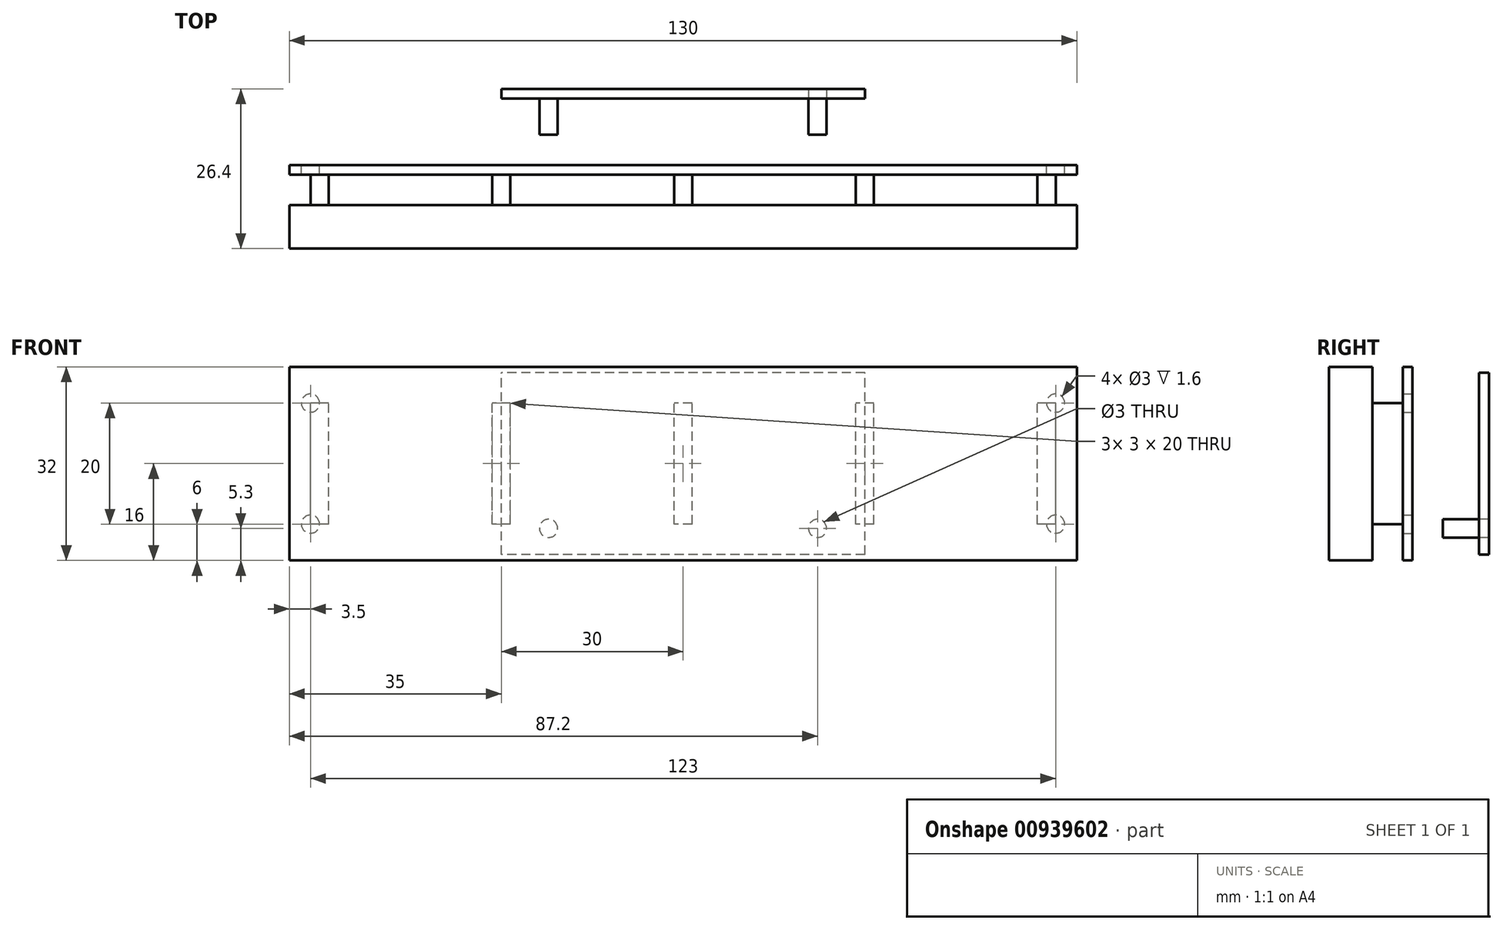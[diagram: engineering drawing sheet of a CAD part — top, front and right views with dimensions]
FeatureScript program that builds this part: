
annotation { "Feature Type Name" : "Feature", "Feature Type Description" : "" }
export const myFeature = defineFeature(function(context is Context, id is Id, definition is map)
    precondition{}
    {
        {
            var Q0;
            Q0=qCreatedBy(makeId("Front.planeOp"),FACE);
            var sketch = newSketch(context, id + "F0", { "sketchPlane" : qUnion([Q0])});
            skLineSegment(sketch, "E0.bottom", {"start": v(65, 16) * mm, "end": v(-65, 16) * mm});
            skLineSegment(sketch, "E0.top", {"start": v(65, -16) * mm, "end": v(-65, -16) * mm});
            skLineSegment(sketch, "E0.left", {"start": v(65, 16) * mm, "end": v(65, -16) * mm});
            skLineSegment(sketch, "E0.right", {"start": v(-65, 16) * mm, "end": v(-65, -16) * mm});
            skPoint(sketch, "E0.middle", {"position": v(0, 0) * mm});
            skSolve(sketch);
        }
        {
            var Q0;
            Q0=makeQuery(id+"F0.imprint","IMPRINT",FACE,{"disambiguationData":[TD([[makeQuery(id+"F0.imprint","IMPRINT",EDGE,{"derivedFrom":sQuery(id+"F0.wireOp",EDGE,"E0.bottom")}),1.0]])]});
            extrude(context, id + "F1", {"entities" : qUnion([Q0]), "depth" : 1.6 * mm, "offsetDistance" : 25 * mm});
        }
        {
            var Q0;
            Q0=makeQuery(id+"F1.opExtrude","CAP_FACE",FACE,{"disambiguationData":[OSD([sQuery(id+"F0.wireOp",EDGE,"E0.bottom"),sQuery(id+"F0.wireOp",EDGE,"E0.top"),sQuery(id+"F0.wireOp",EDGE,"E0.left"),sQuery(id+"F0.wireOp",EDGE,"E0.right")])],"isStart":false});
            var sketch = newSketch(context, id + "F2", { "sketchPlane" : qUnion([Q0])});
            skLineSegment(sketch, "E1.bottom", {"start": v(1.5, -10) * mm, "end": v(-1.5, -10) * mm});
            skLineSegment(sketch, "E1.top", {"start": v(1.5, 10) * mm, "end": v(-1.5, 10) * mm});
            skLineSegment(sketch, "E1.left", {"start": v(1.5, -10) * mm, "end": v(1.5, 10) * mm});
            skLineSegment(sketch, "E1.right", {"start": v(-1.5, -10) * mm, "end": v(-1.5, 10) * mm});
            skPoint(sketch, "E1.middle", {"position": v(0, 0) * mm});
            skLineSegment(sketch, "E2.1.0.0", {"start": v(31.5, -10) * mm, "end": v(31.5, 10) * mm});
            skLineSegment(sketch, "E2.1.0.1", {"start": v(31.5, 10) * mm, "end": v(28.5, 10) * mm});
            skLineSegment(sketch, "E2.1.0.2", {"start": v(28.5, -10) * mm, "end": v(28.5, 10) * mm});
            skLineSegment(sketch, "E2.1.0.3", {"start": v(31.5, -10) * mm, "end": v(28.5, -10) * mm});
            skLineSegment(sketch, "E2.2.0.0", {"start": v(61.5, -10) * mm, "end": v(61.5, 10) * mm});
            skLineSegment(sketch, "E2.2.0.1", {"start": v(61.5, 10) * mm, "end": v(58.5, 10) * mm});
            skLineSegment(sketch, "E2.2.0.2", {"start": v(58.5, -10) * mm, "end": v(58.5, 10) * mm});
            skLineSegment(sketch, "E2.2.0.3", {"start": v(61.5, -10) * mm, "end": v(58.5, -10) * mm});
            skLineSegment(sketch, "E2.direction1", {"start": v(1.5, -10) * mm, "end": v(31.5, -10) * mm, "construction": true});
            skLineSegment(sketch, "E3.1.0.0", {"start": v(-28.5, -10) * mm, "end": v(-28.5, 10) * mm});
            skLineSegment(sketch, "E3.1.0.1", {"start": v(-28.5, 10) * mm, "end": v(-31.5, 10) * mm});
            skLineSegment(sketch, "E3.1.0.2", {"start": v(-31.5, -10) * mm, "end": v(-31.5, 10) * mm});
            skLineSegment(sketch, "E3.1.0.3", {"start": v(-28.5, -10) * mm, "end": v(-31.5, -10) * mm});
            skLineSegment(sketch, "E3.2.0.0", {"start": v(-58.5, -10) * mm, "end": v(-58.5, 10) * mm});
            skLineSegment(sketch, "E3.2.0.1", {"start": v(-58.5, 10) * mm, "end": v(-61.5, 10) * mm});
            skLineSegment(sketch, "E3.2.0.2", {"start": v(-61.5, -10) * mm, "end": v(-61.5, 10) * mm});
            skLineSegment(sketch, "E3.2.0.3", {"start": v(-58.5, -10) * mm, "end": v(-61.5, -10) * mm});
            skLineSegment(sketch, "E3.direction1", {"start": v(1.5, -10) * mm, "end": v(-28.5, -10) * mm, "construction": true});
            skSolve(sketch);
        }
        {
            var Q0;
            Q0=makeQuery(id+"F2.imprint","IMPRINT",FACE,{"disambiguationData":[TD([[makeQuery(id+"F2.imprint","IMPRINT",EDGE,{"derivedFrom":sQuery(id+"F2.wireOp",EDGE,"E1.bottom")}),-1.0]])]});
            var Q1;
            Q1=makeQuery(id+"F2.imprint","IMPRINT",FACE,{"disambiguationData":[TD([[makeQuery(id+"F2.imprint","IMPRINT",EDGE,{"derivedFrom":sQuery(id+"F2.wireOp",EDGE,"E3.2.0.0")}),1.0]])]});
            var Q2;
            Q2=makeQuery(id+"F2.imprint","IMPRINT",FACE,{"disambiguationData":[TD([[makeQuery(id+"F2.imprint","IMPRINT",EDGE,{"derivedFrom":sQuery(id+"F2.wireOp",EDGE,"E3.1.0.0")}),1.0]])]});
            var Q3;
            Q3=makeQuery(id+"F2.imprint","IMPRINT",FACE,{"disambiguationData":[TD([[makeQuery(id+"F2.imprint","IMPRINT",EDGE,{"derivedFrom":sQuery(id+"F2.wireOp",EDGE,"E2.1.0.0")}),1.0]])]});
            var Q4;
            Q4=makeQuery(id+"F2.imprint","IMPRINT",FACE,{"disambiguationData":[TD([[makeQuery(id+"F2.imprint","IMPRINT",EDGE,{"derivedFrom":sQuery(id+"F2.wireOp",EDGE,"E2.2.0.0")}),1.0]])]});
            extrude(context, id + "F3", {"entities" : qUnion([Q0, Q1, Q2, Q3, Q4]), "operationType" : NewBodyOperationType.ADD, "depth" : 5 * mm, "offsetDistance" : 25 * mm});
        }
        {
            var Q0;
            Q0=makeQuery(id+"F3.opExtrude","CAP_FACE",FACE,{"disambiguationData":[OSD([sQuery(id+"F2.wireOp",EDGE,"E1.bottom"),sQuery(id+"F2.wireOp",EDGE,"E1.top"),sQuery(id+"F2.wireOp",EDGE,"E1.left"),sQuery(id+"F2.wireOp",EDGE,"E1.right")])],"isStart":false});
            cPlane(context, id + "F4", {"entities" : qUnion([Q0]), "cplaneType" : CPlaneType.OFFSET, "offset" : 0 * mm, "width" : 150 * mm, "height" : 150 * mm});
        }
        {
            var Q0;
            Q0=qCreatedBy(id+"F4.planeOp",FACE);
            var sketch = newSketch(context, id + "F5", { "sketchPlane" : qUnion([Q0])});
            skLineSegment(sketch, "E4.bottom", {"start": v(65, 16) * mm, "end": v(-65, 16) * mm});
            skLineSegment(sketch, "E4.top", {"start": v(65, -16) * mm, "end": v(-65, -16) * mm});
            skLineSegment(sketch, "E4.left", {"start": v(65, 16) * mm, "end": v(65, -16) * mm});
            skLineSegment(sketch, "E4.right", {"start": v(-65, 16) * mm, "end": v(-65, -16) * mm});
            skPoint(sketch, "E4.middle", {"position": v(0, 0) * mm});
            skSolve(sketch);
        }
        {
            var Q0;
            Q0=makeQuery(id+"F5.imprint","IMPRINT",FACE,{"disambiguationData":[TD([[makeQuery(id+"F5.imprint","IMPRINT",EDGE,{"derivedFrom":sQuery(id+"F5.wireOp",EDGE,"E4.bottom")}),1.0]])]});
            extrude(context, id + "F6", {"entities" : qUnion([Q0]), "operationType" : NewBodyOperationType.ADD, "depth" : 7.2 * mm, "offsetDistance" : 25 * mm});
        }
        {
            var Q0;
            Q0=makeQuery(id+"F1.opExtrude","CAP_FACE",FACE,{"disambiguationData":[OSD([sQuery(id+"F0.wireOp",EDGE,"E0.bottom"),sQuery(id+"F0.wireOp",EDGE,"E0.top"),sQuery(id+"F0.wireOp",EDGE,"E0.left"),sQuery(id+"F0.wireOp",EDGE,"E0.right")])],"isStart":true});
            var sketch = newSketch(context, id + "F7", { "sketchPlane" : qUnion([Q0])});
            skLineSegment(sketch, "E5.bottom", {"start": v(61.5, 10) * mm, "end": v(-61.5, 10) * mm, "construction": true});
            skLineSegment(sketch, "E5.top", {"start": v(61.5, -10) * mm, "end": v(-61.5, -10) * mm, "construction": true});
            skLineSegment(sketch, "E5.left", {"start": v(61.5, 10) * mm, "end": v(61.5, -10) * mm, "construction": true});
            skLineSegment(sketch, "E5.right", {"start": v(-61.5, 10) * mm, "end": v(-61.5, -10) * mm, "construction": true});
            skPoint(sketch, "E5.middle", {"position": v(0, 0) * mm});
            skPoint(sketch, "E6", {"position": v(-61.5, 10) * mm});
            skPoint(sketch, "E7", {"position": v(-61.5, -10) * mm});
            skPoint(sketch, "E8", {"position": v(61.5, 10) * mm});
            skPoint(sketch, "E9", {"position": v(61.5, -10) * mm});
            skCircle(sketch, "E10", {"center": v(-61.5, 10) * mm, "radius": 1.5 * mm});
            skCircle(sketch, "E11", {"center": v(61.5, 10) * mm, "radius": 1.5 * mm});
            skCircle(sketch, "E12", {"center": v(61.5, -10) * mm, "radius": 1.5 * mm});
            skCircle(sketch, "E13", {"center": v(-61.5, -10) * mm, "radius": 1.5 * mm});
            skSolve(sketch);
        }
        {
            var Q0;
            Q0=makeQuery(id+"F7.imprint","IMPRINT",FACE,{"disambiguationData":[TD([[makeQuery(id+"F7.imprint","IMPRINT",EDGE,{"derivedFrom":sQuery(id+"F7.wireOp",EDGE,"E11")}),1.0]])]});
            var Q1;
            Q1=makeQuery(id+"F7.imprint","IMPRINT",FACE,{"disambiguationData":[TD([[makeQuery(id+"F7.imprint","IMPRINT",EDGE,{"derivedFrom":sQuery(id+"F7.wireOp",EDGE,"E12")}),1.0]])]});
            var Q2;
            Q2=makeQuery(id+"F7.imprint","IMPRINT",FACE,{"disambiguationData":[TD([[makeQuery(id+"F7.imprint","IMPRINT",EDGE,{"derivedFrom":sQuery(id+"F7.wireOp",EDGE,"E10")}),1.0]])]});
            var Q3;
            Q3=makeQuery(id+"F7.imprint","IMPRINT",FACE,{"disambiguationData":[TD([[makeQuery(id+"F7.imprint","IMPRINT",EDGE,{"derivedFrom":sQuery(id+"F7.wireOp",EDGE,"E13")}),1.0]])]});
            var Q4;
            Q4=makeQuery(id+"F1.opExtrude","CAP_FACE",FACE,{"disambiguationData":[OSD([sQuery(id+"F0.wireOp",EDGE,"E0.bottom"),sQuery(id+"F0.wireOp",EDGE,"E0.top"),sQuery(id+"F0.wireOp",EDGE,"E0.left"),sQuery(id+"F0.wireOp",EDGE,"E0.right")])],"isStart":false});
            extrude(context, id + "F8", {"entities" : qUnion([Q0, Q1, Q2, Q3]), "operationType" : NewBodyOperationType.REMOVE, "endBound" : BoundingType.UP_TO_SURFACE, "oppositeDirection" : true, "depth" : 25 * mm, "endBoundEntityFace" : qUnion([Q4]), "offsetDistance" : 25 * mm});
        }
        {
            assignVariable(context, id + "F9", {"name" : "offset_z", "anyValue" : 5});
        }
        {
            var Q0;
            Q0=makeQuery(id+"F1.opExtrude","CAP_FACE",FACE,{"disambiguationData":[OSD([sQuery(id+"F0.wireOp",EDGE,"E0.bottom"),sQuery(id+"F0.wireOp",EDGE,"E0.top"),sQuery(id+"F0.wireOp",EDGE,"E0.left"),sQuery(id+"F0.wireOp",EDGE,"E0.right")])],"isStart":true});
            cPlane(context, id + "F10", {"entities" : qUnion([Q0]), "cplaneType" : CPlaneType.OFFSET, "offset" : (getVariable(context, 'offset_z')) * mm, "width" : 150 * mm, "height" : 150 * mm});
        }
        {
            var Q0;
            Q0=qCreatedBy(id+"F10.planeOp",FACE);
            var sketch = newSketch(context, id + "F11", { "sketchPlane" : qUnion([Q0])});
            skPoint(sketch, "E14", {"position": v(0, 0) * mm});
            skLineSegment(sketch, "E15.bottom", {"start": v(24.25, 12.75) * mm, "end": v(-24.25, 12.75) * mm});
            skLineSegment(sketch, "E15.top", {"start": v(24.25, -12.75) * mm, "end": v(-24.25, -12.75) * mm});
            skLineSegment(sketch, "E15.left", {"start": v(24.25, 12.75) * mm, "end": v(24.25, -12.75) * mm});
            skLineSegment(sketch, "E16.left", {"start": v(-25.25, 4) * mm, "end": v(-25.25, -4) * mm});
            skPoint(sketch, "E16.middle", {"position": v(-34.25, 0) * mm});
            skLineSegment(sketch, "E17", {"start": v(-24.25, 12.75) * mm, "end": v(-24.25, 4.01) * mm});
            skLineSegment(sketch, "E18", {"start": v(-24.25, 4.01) * mm, "end": v(-25.25, 4) * mm});
            skLineSegment(sketch, "E19", {"start": v(-24.25, -12.75) * mm, "end": v(-24.25, -4) * mm});
            skLineSegment(sketch, "E20", {"start": v(-25.25, -4) * mm, "end": v(-24.25, -4) * mm});
            skSolve(sketch);
        }
        {
            var Q0;
            {var subQ1=sQuery(id+"F11.wireOp",EDGE,"E15.bottom");Q0=makeQuery(id+"F11.imprint","IMPRINT",FACE,{"disambiguationData":[TD([[makeQuery(id+"F11.imprint","IMPRINT",EDGE,{"derivedFrom":subQ1}),1.0]])]});}
            var Q1;
            {var subQ5=sQuery(id+"F11.wireOp",EDGE,"E16.left");Q1=makeQuery(id+"F11.imprint","IMPRINT",FACE,{"disambiguationData":[TD([[makeQuery(id+"F11.imprint","IMPRINT",EDGE,{"derivedFrom":subQ5}),1.0]])]});}
            extrude(context, id + "F12", {"entities" : qUnion([Q0, Q1]), "depth" : 6 * mm, "offsetDistance" : 25 * mm});
        }
        {
            var Q0;
            Q0=makeQuery(id+"F12.opExtrude","CAP_FACE",FACE,{"disambiguationData":[OSD([sQuery(id+"F11.wireOp",EDGE,"E15.bottom"),sQuery(id+"F11.wireOp",EDGE,"E15.top"),sQuery(id+"F11.wireOp",EDGE,"E15.left"),sQuery(id+"F11.wireOp",EDGE,"E16.left"),sQuery(id+"F11.wireOp",EDGE,"E17"),sQuery(id+"F11.wireOp",EDGE,"E18"),sQuery(id+"F11.wireOp",EDGE,"E19"),sQuery(id+"F11.wireOp",EDGE,"E20")])],"isStart":false});
            var sketch = newSketch(context, id + "F13", { "sketchPlane" : qUnion([Q0])});
            skCircle(sketch, "E21", {"center": v(22.2, 10.7) * mm, "radius": 1.5 * mm});
            skCircle(sketch, "E22.MirrorC", {"center": v(22.2, -10.7) * mm, "radius": 1.5 * mm});
            skCircle(sketch, "E23", {"center": v(-22.2, 10.7) * mm, "radius": 1.5 * mm});
            skCircle(sketch, "E24.MirrorC", {"center": v(-22.2, -10.7) * mm, "radius": 1.5 * mm});
            skSolve(sketch);
        }
        {
            var Q0;
            Q0=makeQuery(id+"F13.imprint","IMPRINT",FACE,{"disambiguationData":[TD([[makeQuery(id+"F13.imprint","IMPRINT",EDGE,{"derivedFrom":sQuery(id+"F13.wireOp",EDGE,"E23")}),1.0]])]});
            var Q1;
            Q1=makeQuery(id+"F13.imprint","IMPRINT",FACE,{"disambiguationData":[TD([[makeQuery(id+"F13.imprint","IMPRINT",EDGE,{"derivedFrom":sQuery(id+"F13.wireOp",EDGE,"E24.MirrorC")}),-1.0]])]});
            var Q2;
            Q2=makeQuery(id+"F13.imprint","IMPRINT",FACE,{"disambiguationData":[TD([[makeQuery(id+"F13.imprint","IMPRINT",EDGE,{"derivedFrom":sQuery(id+"F13.wireOp",EDGE,"E22.MirrorC")}),-1.0]])]});
            var Q3;
            Q3=makeQuery(id+"F13.imprint","IMPRINT",FACE,{"disambiguationData":[TD([[makeQuery(id+"F13.imprint","IMPRINT",EDGE,{"derivedFrom":sQuery(id+"F13.wireOp",EDGE,"E21")}),1.0]])]});
            var Q4;
            Q4=makeQuery(id+"F12.opExtrude","CAP_FACE",FACE,{"disambiguationData":[OSD([sQuery(id+"F11.wireOp",EDGE,"E15.bottom"),sQuery(id+"F11.wireOp",EDGE,"E15.top"),sQuery(id+"F11.wireOp",EDGE,"E15.left"),sQuery(id+"F11.wireOp",EDGE,"E16.left"),sQuery(id+"F11.wireOp",EDGE,"E17"),sQuery(id+"F11.wireOp",EDGE,"E18"),sQuery(id+"F11.wireOp",EDGE,"E19"),sQuery(id+"F11.wireOp",EDGE,"E20")])],"isStart":true});
            extrude(context, id + "F14", {"entities" : qUnion([Q0, Q1, Q2, Q3]), "operationType" : NewBodyOperationType.REMOVE, "endBound" : BoundingType.UP_TO_SURFACE, "oppositeDirection" : true, "depth" : 25 * mm, "endBoundEntityFace" : qUnion([Q4]), "offsetDistance" : 25 * mm});
        }
        {
            var Q0;
            Q0=makeQuery(id+"F12.opExtrude","CAP_FACE",FACE,{"disambiguationData":[OSD([sQuery(id+"F11.wireOp",EDGE,"E15.bottom"),sQuery(id+"F11.wireOp",EDGE,"E15.top"),sQuery(id+"F11.wireOp",EDGE,"E15.left"),sQuery(id+"F11.wireOp",EDGE,"E16.left"),sQuery(id+"F11.wireOp",EDGE,"E17"),sQuery(id+"F11.wireOp",EDGE,"E18"),sQuery(id+"F11.wireOp",EDGE,"E19"),sQuery(id+"F11.wireOp",EDGE,"E20")])],"isStart":false});
            var sketch = newSketch(context, id + "F15", { "sketchPlane" : qUnion([Q0])});
            skLineSegment(sketch, "E25.bottom", {"start": v(-30, -15) * mm, "end": v(30, -15) * mm});
            skLineSegment(sketch, "E25.top", {"start": v(-30, 15) * mm, "end": v(30, 15) * mm});
            skLineSegment(sketch, "E25.left", {"start": v(-30, -15) * mm, "end": v(-30, 15) * mm});
            skLineSegment(sketch, "E25.right", {"start": v(30, -15) * mm, "end": v(30, 15) * mm});
            skPoint(sketch, "E25.middle", {"position": v(0, 0) * mm});
            skSolve(sketch);
        }
        {
            var Q0;
            {var subQ0=sQuery(id+"F15.wireOp",EDGE,"E25.left");Q0=makeQuery(id+"F15.imprint","IMPRINT",FACE,{"disambiguationData":[TD([[makeQuery(id+"F15.imprint","IMPRINT",EDGE,{"derivedFrom":subQ0}),-1.0]])]});}
            var Q1;
            Q1=makeQuery(id+"F15.imprint","IMPRINT",FACE,{"disambiguationData":[TD([[makeQuery(id+"F15.imprint","IMPRINT",EDGE,{"derivedFrom":makeQuery(id+"F12.opExtrude","CAP_EDGE",EDGE,{"disambiguationData":[OSD([sQuery(id+"F11.wireOp",EDGE,"E16.left")])],"isStart":false})}),1.0]])]});
            var Q2;
            {var subQ0=sQuery(id+"F15.wireOp",EDGE,"E25.right");Q2=makeQuery(id+"F15.imprint","IMPRINT",FACE,{"disambiguationData":[TD([[makeQuery(id+"F15.imprint","IMPRINT",EDGE,{"derivedFrom":subQ0}),1.0]])]});}
            extrude(context, id + "F16", {"entities" : qUnion([Q0, Q1, Q2]), "depth" : 1.6 * mm, "offsetDistance" : 25 * mm});
        }
    });
